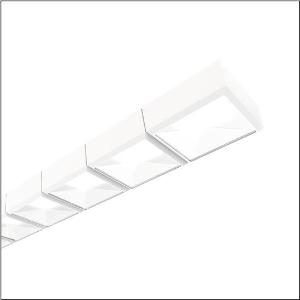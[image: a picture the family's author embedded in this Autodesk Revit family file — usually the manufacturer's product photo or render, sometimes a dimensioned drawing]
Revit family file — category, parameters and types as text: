
# Revit family: scriptus_r__11_5mz212d04wa_64be
name_source: partatom
category: Lighting Fixtures
units: mm (PartAtom-declared; Revit-internal decimal feet)

## family parameters
Cut with Voids When Loaded = No
Host = Face
Light Source = No
Part Type = Normal
Room Calculation Point = No
Round Connector Dimension = Use Diameter
Shared = No

## types (1)
- Scriptus® 11 (1 x LED 4000K / CRI = 80 (unbekannt), 2410 lm, 4000K)
    Apparent Load = 35 VA
    CIE Flux Codes = 82 95 99 100 100
    Color Rendering = 80
    Color Temperature = 4000K
    Default Elevation = 1800 mm
    Description = Scriptus® 11, office luminaire, primary optical cover: lenses, CAT 2 (L<= 3000cd/m²), light emission: direct distribution, primary light characteristic: symmetric, installation type: surface-mounted, LED, rated luminous flux: 4.810lm, luminous efficacy: 139lm/W, light colour: 840, colour temperature: 4000K, control gear: ECG DALI, with terminal, 5-pole, mains connection: 230V, AC, 50Hz, rated input power: 35W, housing, luminaire housing, of aluminium, traffic white (RAL 9016), length: 1.658mm, width: 114mm, height: 57mm, protection rating (complete): IP20, insulation class (complete): insulation class I (protective earthing), certification: CE, ENEC, VDE, protection symbol: F, permissible operating ambient temperature: 0..+35°C, standard: EN 50419, packaging unit: 1 piece
    Height = 57 mm
    Lamp = 1 x LED 4000K / CRI >= 80 (unbekannt)
    Lamp Light Flux = 2410 lm
    Lamp count = 1
    Length = 1658 mm
    Luminous efficacy = 139 lm/W
    Manufacturer = Siteco
    ModVariant = No
    Model = 5MZ212D04WA
    Mounting Place = Ceiling
    Mounting Type = Surface mounted
    Number of Poles = 1
    OnlyDefault = Yes
    Power Factor = 1
    Product Name = Scriptus® 11
    Product group = office luminaire | ceiling mounted
    ProductGroupID = 304
    Protection Class = Protection class I
    Protection Degree = IP 20
    RLX_Detail_Level = 1
    RLX_Emergency_Light_Flux = 0 lm
    RLX_Emergency_Type = 0
    RLX_Emergency_Type_DB = No
    RlxData = <blob elided: 29521 chars, md5=107e28b9>
    Socket = socket
    Standby Power = 0 W
    System Light Flux = 4820 lm
    System Power = 35 W
    Type Comments = Product without accessories
    Type Image = l_1004833.jpg
    URL = http://relux.com
    VarID = ---
    Voltage = 0 V
    Weight = 0.00 kg
    Width = 114 mm

## geometry (parser evidence)
native form markers: Blend x4, Sweep x15
no freeform markers — native parametric forms only
